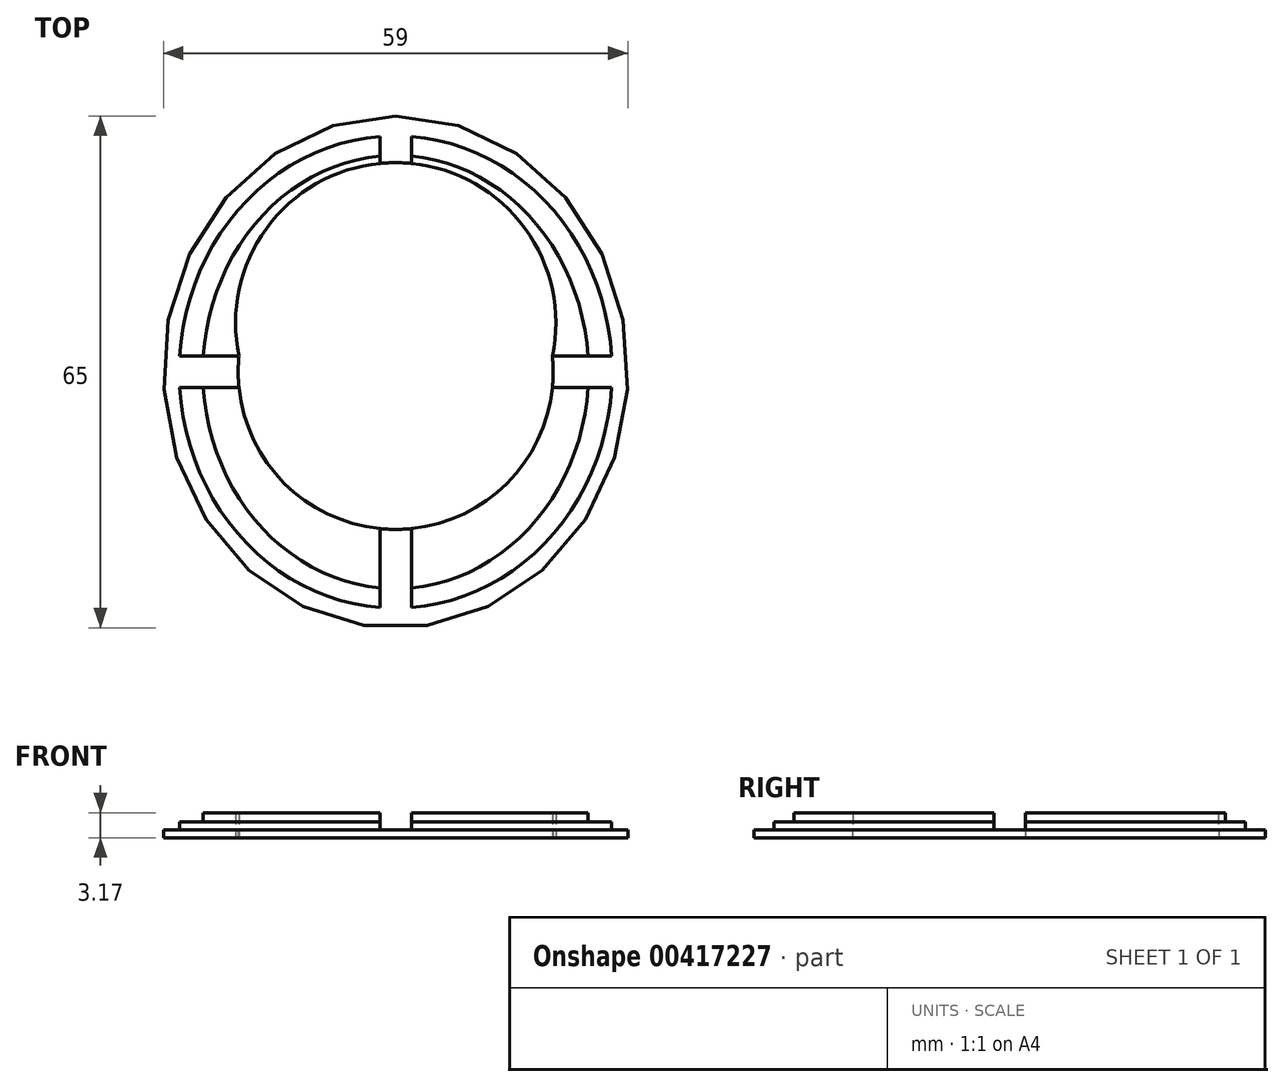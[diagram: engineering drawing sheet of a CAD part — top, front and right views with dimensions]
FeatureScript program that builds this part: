
annotation { "Feature Type Name" : "Feature", "Feature Type Description" : "" }
export const myFeature = defineFeature(function(context is Context, id is Id, definition is map)
    precondition{}
    {
        {
            var Q0;
            Q0=qCreatedBy(makeId("Top.planeOp"),FACE);
            var sketch = newSketch(context, id + "F0", { "sketchPlane" : qUnion([Q0])});
            skEllipse(sketch, "E0", {"center": v(0, 0) * mm, "majorRadius": 29.5 * mm, "minorRadius": 32.5 * mm, "majorAxis": v(1, 0)});
            skArc(sketch, "E1", {"start": v(-19.9, 2) * mm, "mid": v(0, -20) * mm, "end": v(19.9, 2) * mm});
            skLineSegment(sketch, "E2", {"start": v(2, 27.4) * mm, "end": v(2, 26.5) * mm});
            skLineSegment(sketch, "E3", {"start": v(-2, 27.4) * mm, "end": v(-2, 26.5) * mm});
            skLineSegment(sketch, "E4", {"start": v(-24.44, 2) * mm, "end": v(-19.9, 2) * mm});
            skLineSegment(sketch, "E5", {"start": v(-24.44, -2) * mm, "end": v(-19.9, -2) * mm});
            skPoint(sketch, "E6.start.orphan", {"position": v(-29.5, 0) * mm});
            skEllipticalArc(sketch, "E7", {});
            skLineSegment(sketch, "E8.trimOffspring", {"start": v(19.9, 2) * mm, "end": v(24.44, 2) * mm});
            skLineSegment(sketch, "E9.trimOffspring", {"start": v(-2, -19.9) * mm, "end": v(-2, -27.4) * mm});
            skLineSegment(sketch, "E10.trimOffspring", {"start": v(2, -19.9) * mm, "end": v(2, -27.4) * mm});
            skLineSegment(sketch, "E11.trimOffspring", {"start": v(19.9, -2) * mm, "end": v(24.44, -2) * mm});
            skEllipticalArc(sketch, "E12", {});
            skLineSegment(sketch, "E13", {"start": v(-2, 27.4) * mm, "end": v(-2, 29.92) * mm});
            skLineSegment(sketch, "E14", {"start": v(2, 27.4) * mm, "end": v(2, 29.92) * mm});
            skLineSegment(sketch, "E15", {"start": v(24.44, 2) * mm, "end": v(27.44, 2) * mm});
            skLineSegment(sketch, "E16", {"start": v(24.44, -2) * mm, "end": v(27.44, -2) * mm});
            skLineSegment(sketch, "E17", {"start": v(-24.44, 2) * mm, "end": v(-27.44, 2) * mm});
            skLineSegment(sketch, "E18", {"start": v(-24.44, -2) * mm, "end": v(-27.44, -2) * mm});
            skLineSegment(sketch, "E19", {"start": v(2, -27.4) * mm, "end": v(2, -29.92) * mm});
            skLineSegment(sketch, "E20", {"start": v(-2, -27.4) * mm, "end": v(-2, -29.92) * mm});
            skEllipticalArc(sketch, "E21.trimOffspring", {});
            skEllipticalArc(sketch, "E22.trimOffspring", {});
            skEllipticalArc(sketch, "E23.trimOffspring", {});
            skEllipticalArc(sketch, "E24.trimOffspring", {});
            skEllipticalArc(sketch, "E25.trimOffspring", {});
            skEllipticalArc(sketch, "E26.trimOffspring", {});
            skArc(sketch, "E27", {"start": v(19.9, 2) * mm, "mid": v(0, 26.6) * mm, "end": v(-19.9, 2) * mm});
            const initialGuessF0  = {"E7": [0, 0, 1, 0, 0.0245, 0.0275, 1.6525199179924037, 3.068801115586383], "E12": [0, 0, 1, 0, 0.0275, 0.03, 1.6435878647983069, 3.074876505179568], "E21.trimOffspring": [0, 0, 1, 0, 0.0245, 0.0275, 0.07279153800341032, 1.4890727355973894], "E22.trimOffspring": [0, 0, 1, 0, 0.0275, 0.03, 0.066716148410225, 1.4980047887914862], "E23.trimOffspring": [0, 0, 1, 0, 0.0275, 0.03, 4.785180518388099, 6.21646915876936], "E24.trimOffspring": [0, 0, 1, 0, 0.0245, 0.0275, 4.794112571582195, 6.210393769176176], "E25.trimOffspring": [0, 0, 1, 0, 0.0245, 0.0275, 3.2143841915932034, 4.6306653891871825], "E26.trimOffspring": [0, 0, 1, 0, 0.0275, 0.03, 3.2083088020000186, 4.639597442381279]};
            skSetInitialGuess(sketch, initialGuessF0);
            skSolve(sketch);
        }
        {
            var Q0;
            Q0=makeQuery(id+"F0.imprint","IMPRINT",FACE,{"disambiguationData":[TD([[makeQuery(id+"F0.imprint","IMPRINT",EDGE,{"derivedFrom":sQuery(id+"F0.wireOp",EDGE,"E0")}),1.0]])]});
            extrude(context, id + "F1", {"entities" : qUnion([Q0]), "depth" : 1 * mm});
        }
        {
            var Q0;
            Q0=makeQuery(id+"F0.imprint","IMPRINT",FACE,{"disambiguationData":[TD([[makeQuery(id+"F0.imprint","IMPRINT",EDGE,{"derivedFrom":sQuery(id+"F0.wireOp",EDGE,"E7")}),-1.0]])]});
            var Q1;
            Q1=makeQuery(id+"F0.imprint","IMPRINT",FACE,{"disambiguationData":[TD([[makeQuery(id+"F0.imprint","IMPRINT",EDGE,{"derivedFrom":sQuery(id+"F0.wireOp",EDGE,"E14")}),-1.0]])]});
            var Q2;
            Q2=makeQuery(id+"F0.imprint","IMPRINT",FACE,{"disambiguationData":[TD([[makeQuery(id+"F0.imprint","IMPRINT",EDGE,{"derivedFrom":sQuery(id+"F0.wireOp",EDGE,"E16")}),-1.0]])]});
            var Q3;
            Q3=makeQuery(id+"F0.imprint","IMPRINT",FACE,{"disambiguationData":[TD([[makeQuery(id+"F0.imprint","IMPRINT",EDGE,{"derivedFrom":sQuery(id+"F0.wireOp",EDGE,"E18")}),1.0]])]});
            extrude(context, id + "F2", {"entities" : qUnion([Q0, Q1, Q2, Q3]), "operationType" : NewBodyOperationType.ADD, "depth" : 2 * mm});
        }
        {
            var Q0;
            {var subQ0=sQuery(id+"F0.wireOp",EDGE,"E3");Q0=makeQuery(id+"F0.imprint","IMPRINT",FACE,{"disambiguationData":[TD([[makeQuery(id+"F0.imprint","IMPRINT",EDGE,{"derivedFrom":subQ0}),-1.0]])]});}
            var Q1;
            {var subQ0=sQuery(id+"F0.wireOp",EDGE,"E2");Q1=makeQuery(id+"F0.imprint","IMPRINT",FACE,{"disambiguationData":[TD([[makeQuery(id+"F0.imprint","IMPRINT",EDGE,{"derivedFrom":subQ0}),1.0]])]});}
            var Q2;
            {var subQ0=sQuery(id+"F0.wireOp",EDGE,"E10.trimOffspring");Q2=makeQuery(id+"F0.imprint","IMPRINT",FACE,{"disambiguationData":[TD([[makeQuery(id+"F0.imprint","IMPRINT",EDGE,{"derivedFrom":subQ0}),1.0]])]});}
            var Q3;
            {var subQ0=sQuery(id+"F0.wireOp",EDGE,"E5");Q3=makeQuery(id+"F0.imprint","IMPRINT",FACE,{"disambiguationData":[TD([[makeQuery(id+"F0.imprint","IMPRINT",EDGE,{"derivedFrom":subQ0}),-1.0]])]});}
            extrude(context, id + "F3", {"entities" : qUnion([Q0, Q1, Q2, Q3]), "operationType" : NewBodyOperationType.ADD, "depth" : 3.17 * mm});
        }
    });
